# Revit family: IAQ-PURGE2
name_source: partatom
category: Mechanical Equipment
revit_build: Autodesk Revit 2015 (Build: 20140606_1530(x64)
units: mm (PartAtom-declared; Revit-internal decimal feet)

## types (1)
- IAQ-PURGE2
    Apparent Load = 253 VA
    Classification.Uniclass.Pr.Description = Centrifugal fans
    Classification.Uniclass.Pr.Number = Pr_65_67_29_12
    Description = Inline Purge Fan with 3 speeds
    Electrical Phase = 1
    Fan Unit = Yes
    Fax Number = +44(0)2920-858-222
    Full Load Current = 1 A
    Height = 150 mm
    I&M Manual = http://www.nuaire.info
    IFCExportAs = IfcFanType
    Manufacturer = Nuaire
    Manufacturer Name = Nuaire
    Maximum Ambient Temperature = 40 °C
    Model = IAQ-PURGE
    Nuaire Model No = IAQ-PURGE
    Number of Connection Poles = 2
    OmniClass Number = 23-33 31 19 13
    OmniClass Title = Centrifugal Fans
    Postcode = CF83 1NA
    Revit Family Last Revised = 26/02/19
    Spigot Height = 90 mm  [stored 0.295276 ft]
    Spigot Width = 220 mm  [stored 0.721785 ft]
    Starting Current = 1 A
    Supplier Part No = IAQ-PURGE
    Telephone Number = +44(0)2920-858-200
    Type Comments = 1
    URL = http://www.nuaire.co.uk
    Unit Description = Inline Purge Fan with 3 speeds
    VAT Registration Number = 877308
    Voltage = 230 V
    Warranty Period = 5 Years
    Weatherproof or Internal Only = Internal
    Weight = 7.00 kg

note: [stored X ft] marks values corroborated as IEEE doubles in the binary element streams (Revit-internal decimal feet)

## geometry (parser evidence)
native form markers: Blend x30, Sweep x4
no freeform markers — native parametric forms only
